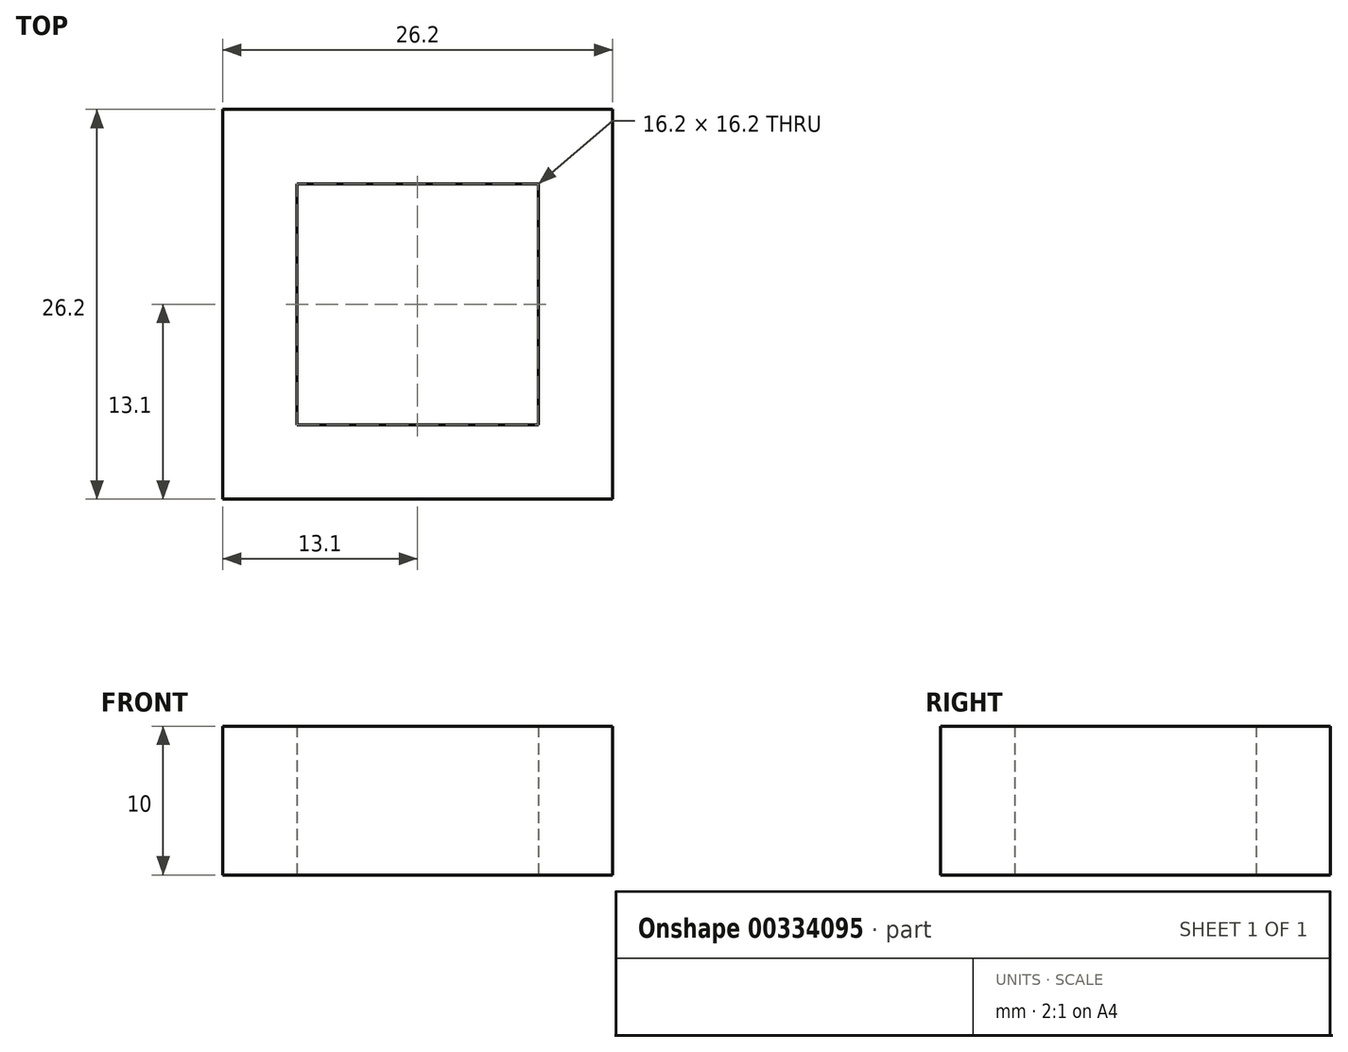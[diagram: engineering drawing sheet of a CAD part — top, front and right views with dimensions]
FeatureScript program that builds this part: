
annotation { "Feature Type Name" : "Feature", "Feature Type Description" : "" }
export const myFeature = defineFeature(function(context is Context, id is Id, definition is map)
    precondition{}
    {
        {
            var Q0;
            Q0=qCreatedBy(makeId("Top.planeOp"),FACE);
            var sketch = newSketch(context, id + "F0", { "sketchPlane" : qUnion([Q0])});
            skLineSegment(sketch, "E0.bottom", {"start": v(8.1, -8.1) * mm, "end": v(-8.1, -8.1) * mm});
            skLineSegment(sketch, "E0.top", {"start": v(8.1, 8.1) * mm, "end": v(-8.1, 8.1) * mm});
            skLineSegment(sketch, "E0.left", {"start": v(8.1, -8.1) * mm, "end": v(8.1, 8.1) * mm});
            skLineSegment(sketch, "E0.right", {"start": v(-8.1, -8.1) * mm, "end": v(-8.1, 8.1) * mm});
            skPoint(sketch, "E0.middle", {"position": v(0, 0) * mm});
            skLineSegment(sketch, "E1.0", {"start": v(13.1, 13.1) * mm, "end": v(-13.1, 13.1) * mm});
            skLineSegment(sketch, "E1.1", {"start": v(13.1, -13.1) * mm, "end": v(13.1, 13.1) * mm});
            skLineSegment(sketch, "E1.2", {"start": v(13.1, -13.1) * mm, "end": v(-13.1, -13.1) * mm});
            skLineSegment(sketch, "E1.3", {"start": v(-13.1, -13.1) * mm, "end": v(-13.1, 13.1) * mm});
            skSolve(sketch);
        }
        {
            var Q0;
            Q0=makeQuery(id+"F0.imprint","IMPRINT",FACE,{"disambiguationData":[TD([[makeQuery(id+"F0.imprint","IMPRINT",EDGE,{"derivedFrom":sQuery(id+"F0.wireOp",EDGE,"E0.bottom")}),1.0]])]});
            extrude(context, id + "F1", {"entities" : qUnion([Q0]), "depth" : 10 * mm});
        }
    });
